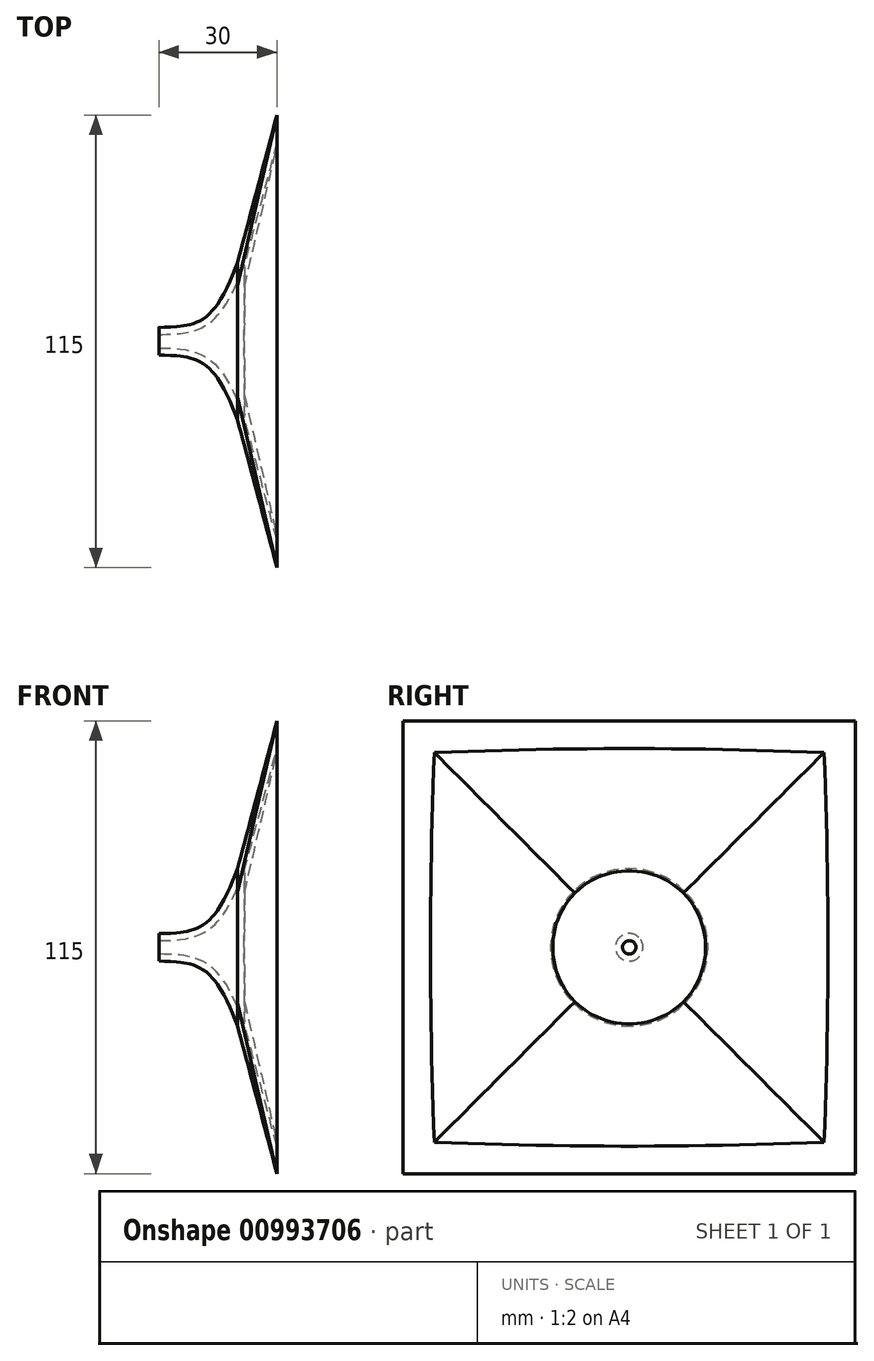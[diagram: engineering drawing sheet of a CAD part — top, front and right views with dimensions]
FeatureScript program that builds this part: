
annotation { "Feature Type Name" : "Feature", "Feature Type Description" : "" }
export const myFeature = defineFeature(function(context is Context, id is Id, definition is map)
    precondition{}
    {
        {
            var Q0;
            Q0=qCreatedBy(makeId("Right.planeOp"),FACE);
            var sketch = newSketch(context, id + "F0", { "sketchPlane" : qUnion([Q0])});
            skCircle(sketch, "E0", {"center": v(0, 0) * mm, "radius": 3.5 * mm});
            skSolve(sketch);
        }
        {
            var Q0;
            Q0=qCreatedBy(makeId("Right.planeOp"),FACE);
            cPlane(context, id + "F1", {"entities" : qUnion([Q0]), "cplaneType" : CPlaneType.OFFSET, "offset" : 10 * mm, "width" : 150 * mm, "height" : 150 * mm});
        }
        {
            var Q0;
            Q0=qCreatedBy(id+"F1.planeOp",FACE);
            var sketch = newSketch(context, id + "F2", { "sketchPlane" : qUnion([Q0])});
            skCircle(sketch, "E1", {"center": v(0, 0) * mm, "radius": 5 * mm});
            skSolve(sketch);
        }
        {
            var Q0;
            Q0=qCreatedBy(id+"F1.planeOp",FACE);
            cPlane(context, id + "F3", {"entities" : qUnion([Q0]), "cplaneType" : CPlaneType.OFFSET, "offset" : 10 * mm, "width" : 150 * mm, "height" : 150 * mm});
        }
        {
            var Q0;
            Q0=qCreatedBy(id+"F3.planeOp",FACE);
            var sketch = newSketch(context, id + "F4", { "sketchPlane" : qUnion([Q0])});
            skCircle(sketch, "E2", {"center": v(0, 0) * mm, "radius": 20 * mm});
            skSolve(sketch);
        }
        {
            var Q0;
            Q0=qCreatedBy(id+"F3.planeOp",FACE);
            cPlane(context, id + "F5", {"entities" : qUnion([Q0]), "cplaneType" : CPlaneType.OFFSET, "offset" : 10 * mm, "width" : 150 * mm, "height" : 150 * mm});
        }
        {
            var Q0;
            Q0=qCreatedBy(id+"F5.planeOp",FACE);
            var sketch = newSketch(context, id + "F6", { "sketchPlane" : qUnion([Q0])});
            skLineSegment(sketch, "E3.bottom", {"start": v(-57.5, 57.5) * mm, "end": v(57.5, 57.5) * mm});
            skLineSegment(sketch, "E3.top", {"start": v(-57.5, -57.5) * mm, "end": v(57.5, -57.5) * mm});
            skLineSegment(sketch, "E3.left", {"start": v(-57.5, 57.5) * mm, "end": v(-57.5, -57.5) * mm});
            skLineSegment(sketch, "E3.right", {"start": v(57.5, 57.5) * mm, "end": v(57.5, -57.5) * mm});
            skPoint(sketch, "E3.middle", {"position": v(0, 0) * mm});
            skSolve(sketch);
        }
        {
            var Q0;
            Q0=makeQuery(id+"F0.imprint","IMPRINT",FACE,{"disambiguationData":[TD([[makeQuery(id+"F0.imprint","IMPRINT",EDGE,{"derivedFrom":sQuery(id+"F0.wireOp",EDGE,"E0")}),1.0]])]});
            var Q1;
            Q1=makeQuery(id+"F2.imprint","IMPRINT",FACE,{"disambiguationData":[TD([[makeQuery(id+"F2.imprint","IMPRINT",EDGE,{"derivedFrom":sQuery(id+"F2.wireOp",EDGE,"E1")}),1.0]])]});
            var Q2;
            Q2=makeQuery(id+"F4.imprint","IMPRINT",FACE,{"disambiguationData":[TD([[makeQuery(id+"F4.imprint","IMPRINT",EDGE,{"derivedFrom":sQuery(id+"F4.wireOp",EDGE,"E2")}),1.0]])]});
            loft(context, id + "F7", {"sheetProfilesArray" : [{ "sheetProfileEntities" : qUnion([Q0]) }, { "sheetProfileEntities" : qUnion([Q1]) }, { "sheetProfileEntities" : qUnion([Q2]) }]});
        }
        {
            var Q1;
            Q1=makeQuery(id+"F7.opLoft","CAP_FACE",FACE,{"disambiguationData":[OSD([makeQuery(id+"F4.imprint","IMPRINT",FACE,{"disambiguationData":[TD([[makeQuery(id+"F4.imprint","IMPRINT",EDGE,{"derivedFrom":sQuery(id+"F4.wireOp",EDGE,"E2")}),1.0]])]})])],"isStart":true});
            var Q2;
            Q2=makeQuery(id+"F6.imprint","IMPRINT",FACE,{"disambiguationData":[TD([[makeQuery(id+"F6.imprint","IMPRINT",EDGE,{"derivedFrom":sQuery(id+"F6.wireOp",EDGE,"E3.bottom")}),-1.0]])]});
            loft(context, id + "F8", {"operationType" : NewBodyOperationType.ADD, "sheetProfilesArray" : [{ "sheetProfileEntities" : qUnion([Q1]) }, { "sheetProfileEntities" : qUnion([Q2]) }]});
        }
        {
            var Q0;
            Q0=makeQuery(id+"F8.opLoft","CAP_FACE",FACE,{"disambiguationData":[OSD([makeQuery(id+"F6.imprint","IMPRINT",FACE,{"disambiguationData":[TD([[makeQuery(id+"F6.imprint","IMPRINT",EDGE,{"derivedFrom":sQuery(id+"F6.wireOp",EDGE,"E3.bottom")}),-1.0]])]})])],"isStart":true});
            var Q1;
            Q1=makeQuery(id+"F7.opLoft","CAP_FACE",FACE,{"disambiguationData":[OSD([makeQuery(id+"F0.imprint","IMPRINT",FACE,{"disambiguationData":[TD([[makeQuery(id+"F0.imprint","IMPRINT",EDGE,{"derivedFrom":sQuery(id+"F0.wireOp",EDGE,"E0")}),1.0]])]})])],"isStart":true});
            shell(context, id + "F9", {"entities" : qUnion([Q0, Q1]), "thickness" : 1.8 * mm});
        }
    });
